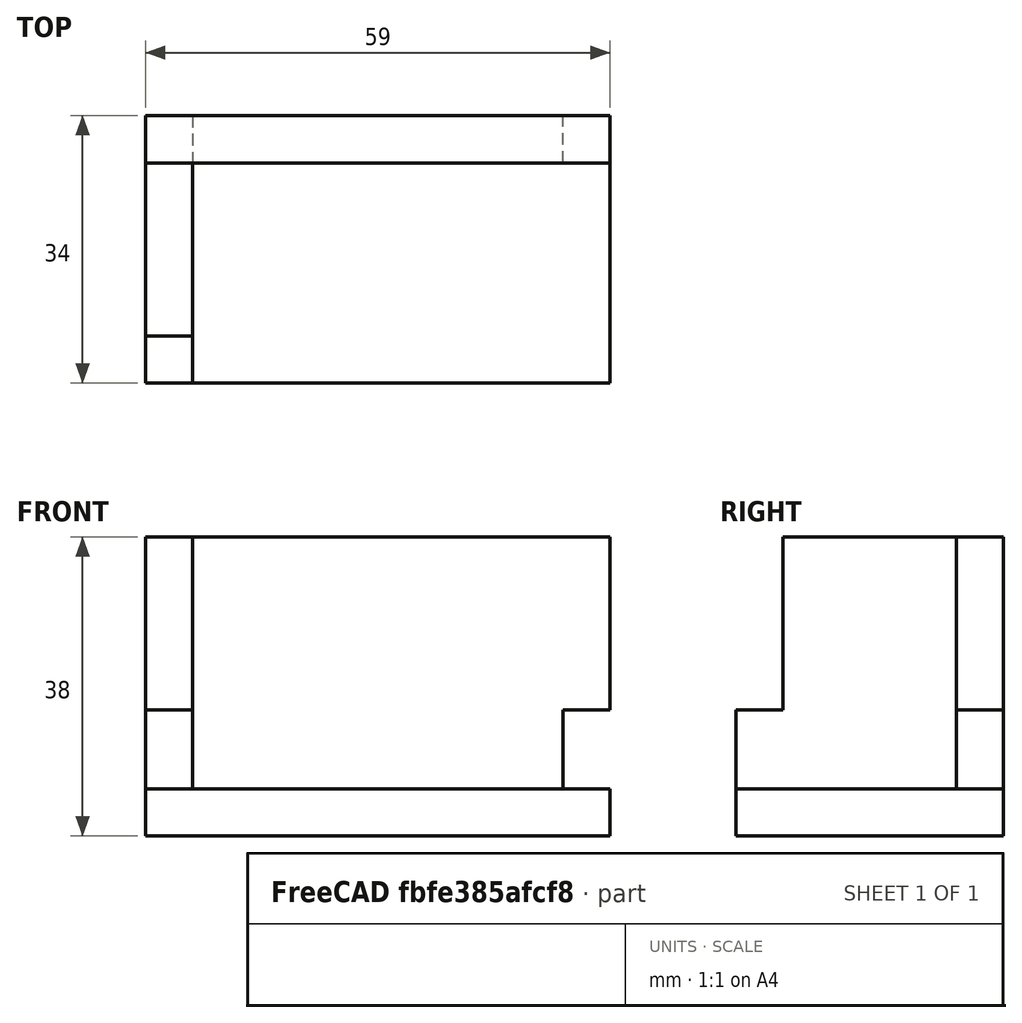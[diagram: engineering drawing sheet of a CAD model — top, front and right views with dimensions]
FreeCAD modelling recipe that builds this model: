
FCSTD DOCUMENT  (FreeCAD 0.18R16146 (Git))
Label: brass birmingham - merchant token tray
License: All rights reserved
LicenseURL: http://en.wikipedia.org/wiki/All_rights_reserved
objects: TechDraw::DrawViewPart×7, Sketcher::SketchObject×5, PartDesign::Body×5, PartDesign::Pad×3, Spreadsheet::Sheet×2, PartDesign::Pocket×2, PartDesign::FeatureBase×2, App::DocumentObjectGroup×2, TechDraw::DrawSVGTemplate×2, TechDraw::DrawViewDimension×2, TechDraw::DrawPage×2
note: 22 computed .brp shape members not serialized (recipe doc carries the construction recipe); baked Part::Feature solids carry a one-line shape summary decoded from their .brp

FEATURE [Spreadsheet::Sheet] Spreadsheet  label="my_variables"
  cells = A1=foam_width; B1(foam_width)==6mm; A2=lower_height; B2(lower_height)==29mm; A3=outer height (minus base); B3(height_adjusted)==38mm - B1; A4=outer long width; B4(width_long)==96mm; A5=outer short width; B5(width_short)==59mm
FEATURE [Sketcher::SketchObject] Sketch
  MapMode = 5
  Support = -> [XY_Plane]
  expr: Constraints[9] = my_variables001.width_short
  expr: Constraints[10] = my_variables001.width_long
  sketch-geometry (4):
    g0: LineSegment StartX=-29.5 StartY=34 StartZ=0 EndX=29.5 EndY=34 EndZ=0
    g1: LineSegment StartX=29.5 StartY=34 StartZ=0 EndX=29.5 EndY=0 EndZ=0
    g2: LineSegment StartX=29.5 StartY=0 StartZ=0 EndX=-29.5 EndY=0 EndZ=0
    g3: LineSegment StartX=-29.5 StartY=0 StartZ=0 EndX=-29.5 EndY=34 EndZ=0
  constraints (11):
    c: Coincident(g0,g1)
    c: Coincident(g1,g2)
    c: Coincident(g2,g3)
    c: Coincident(g3,g0)
    c: Horizontal(g0)
    c: Horizontal(g2)
    c: Vertical(g1)
    c: Vertical(g3)
    c: Symmetric(g2,g2,g-1)
    c: Distance(g3) = 34
    c: Distance(g2) = 59
FEATURE [PartDesign::Pad] Pad
  Length = 6
  Length2 = 100
  Profile = -> Sketch
  Type = 0
  expr: Length = my_variables.foam_width
FEATURE [PartDesign::Body] Body  label="base"
  Group = -> [Sketch,Pad]
  Origin = -> Origin
  Tip = -> Pad
FEATURE [Sketcher::SketchObject] Sketch001
  MapMode = 5
  Placement = pos=(0,0,0) rot=(1,0,0;1.5708rad)
  Support = -> [XZ_Plane001]
  expr: Constraints[10] = my_variables001.width_long
  expr: Constraints[9] = my_variables001.height_adjusted
  sketch-geometry (4):
    g0: LineSegment StartX=-29.5 StartY=32 StartZ=0 EndX=29.5 EndY=32 EndZ=0
    g1: LineSegment StartX=29.5 StartY=32 StartZ=0 EndX=29.5 EndY=0 EndZ=0
    g2: LineSegment StartX=29.5 StartY=0 StartZ=0 EndX=-29.5 EndY=0 EndZ=0
    g3: LineSegment StartX=-29.5 StartY=0 StartZ=0 EndX=-29.5 EndY=32 EndZ=0
  constraints (11):
    c: Coincident(g0,g1)
    c: Coincident(g1,g2)
    c: Coincident(g2,g3)
    c: Coincident(g3,g0)
    c: Horizontal(g0)
    c: Horizontal(g2)
    c: Vertical(g1)
    c: Vertical(g3)
    c: Symmetric(g2,g2,g-1)
    c: Distance(g3) = 32
    c: Distance(g0) = 59
FEATURE [PartDesign::Pad] Pad001
  Length = 6
  Length2 = 100
  Placement = pos=(0,0,0) rot=(1,0,0;1.5708rad)
  Profile = -> Sketch001
  Type = 0
  expr: Length = my_variables.foam_width
FEATURE [Sketcher::SketchObject] Sketch002
  MapMode = 5
  Placement = pos=(0,-6,-1.3e-15) rot=(1,0,0;1.5708rad)
  Support = -> [Pad001]
  expr: Constraints[30] = my_variables.foam_width
  expr: Constraints[29] = my_variables.foam_width
  expr: Constraints[10] = Sketch001.Constraints[10]
  expr: Constraints[9] = Sketch001.Constraints[9]
  sketch-geometry (12):
    g0: LineSegment [constr] StartX=-29.5 StartY=32 StartZ=0 EndX=29.5 EndY=32 EndZ=0
    g1: LineSegment [constr] StartX=29.5 StartY=32 StartZ=0 EndX=29.5 EndY=0 EndZ=0
    g2: LineSegment [constr] StartX=29.5 StartY=0 StartZ=0 EndX=-29.5 EndY=0 EndZ=0
    g3: LineSegment [constr] StartX=-29.5 StartY=0 StartZ=0 EndX=-29.5 EndY=32 EndZ=0
    g4: LineSegment StartX=-29.5 StartY=10 StartZ=0 EndX=-23.5 EndY=10 EndZ=0
    g5: LineSegment StartX=-23.5 StartY=10 StartZ=0 EndX=-23.5 EndY=0 EndZ=0
    g6: LineSegment StartX=-23.5 StartY=0 StartZ=0 EndX=-29.5 EndY=0 EndZ=0
    g7: LineSegment StartX=-29.5 StartY=0 StartZ=0 EndX=-29.5 EndY=10 EndZ=0
    g8: LineSegment StartX=23.5 StartY=10 StartZ=0 EndX=29.5 EndY=10 EndZ=0
    g9: LineSegment StartX=29.5 StartY=10 StartZ=0 EndX=29.5 EndY=0 EndZ=0
    g10: LineSegment StartX=29.5 StartY=0 StartZ=0 EndX=23.5 EndY=0 EndZ=0
    g11: LineSegment StartX=23.5 StartY=0 StartZ=0 EndX=23.5 EndY=10 EndZ=0
  constraints (33):
    c: Coincident(g0,g1)
    c: Coincident(g1,g2)
    c: Coincident(g2,g3)
    c: Coincident(g3,g0)
    c: Horizontal(g0)
    c: Horizontal(g2)
    c: Vertical(g1)
    c: Vertical(g3)
    c: Symmetric(g2,g2,g-1)
    c: Distance(g3) = 32
    c: Distance(g0) = 59
    c: Coincident(g4,g5)
    c: Coincident(g5,g6)
    c: Coincident(g6,g7)
    c: Coincident(g7,g4)
    c: Horizontal(g4)
    c: Horizontal(g6)
    c: Vertical(g5)
    c: Vertical(g7)
    c: Coincident(g8,g9)
    c: Coincident(g9,g10)
    c: Coincident(g10,g11)
    c: Coincident(g11,g8)
    c: Horizontal(g8)
    c: Horizontal(g10)
    c: Vertical(g9)
    c: Vertical(g11)
    c: Coincident(g6,g2)
    c: Coincident(g9,g1)
    c: Distance(g4) = 6
    c: Distance(g8) = 6
    c: Distance(g5) = 10
    c: Distance(g11) = 10
FEATURE [PartDesign::Pocket] Pocket
  BaseFeature = -> Pad001
  Length = 5
  Length2 = 100
  Placement = pos=(0,0,0) rot=(1,0,0;1.5708rad)
  Profile = -> Sketch002
  Type = 1
FEATURE [PartDesign::Body] Body001  label="side long"
  Group = -> [Sketch001,Pad001,Sketch002,Pocket]
  Origin = -> Origin001
  Placement = pos=(7e-15,6,6) rot=(0,0,1;0rad)
  Tip = -> Pocket
FEATURE [PartDesign::FeatureBase] Clone
  BaseFeature = -> Body001
  Placement = pos=(7e-15,6,6) rot=(0,0,1;0rad)
FEATURE [PartDesign::Body] Body002  label="side long - clone"
  BaseFeature = -> Body001
  Group = -> [Clone]
  Origin = -> Origin002
  Placement = pos=(-1.4e-14,28,-1.28e-14) rot=(0,0,1;0rad)
  Tip = -> Clone
FEATURE [Sketcher::SketchObject] Sketch003
  MapMode = 5
  Placement = pos=(0,0,0) rot=(0.57735,0.57735,0.57735;2.0944rad)
  Support = -> [YZ_Plane003]
  expr: Constraints[10] = my_variables001.width_short
  expr: Constraints[9] = my_variables001.height_adjusted
  sketch-geometry (4):
    g0: LineSegment StartX=-17 StartY=32 StartZ=0 EndX=17 EndY=32 EndZ=0
    g1: LineSegment StartX=17 StartY=32 StartZ=0 EndX=17 EndY=0 EndZ=0
    g2: LineSegment StartX=17 StartY=0 StartZ=0 EndX=-17 EndY=0 EndZ=0
    g3: LineSegment StartX=-17 StartY=0 StartZ=0 EndX=-17 EndY=32 EndZ=0
  constraints (11):
    c: Coincident(g0,g1)
    c: Coincident(g1,g2)
    c: Coincident(g2,g3)
    c: Coincident(g3,g0)
    c: Horizontal(g0)
    c: Horizontal(g2)
    c: Vertical(g1)
    c: Vertical(g3)
    c: Symmetric(g2,g2,g-1)
    c: Distance(g3) = 32
    c: Distance(g0) = 34
FEATURE [PartDesign::Pad] Pad002
  Length = 6
  Length2 = 100
  Placement = pos=(0,0,0) rot=(0.57735,0.57735,0.57735;2.0944rad)
  Profile = -> Sketch003
  Type = 0
  expr: Length = my_variables.foam_width
FEATURE [Sketcher::SketchObject] Sketch004
  MapMode = 5
  Placement = pos=(6,-2.7e-15,2e-15) rot=(0.57735,0.57735,0.57735;2.0944rad)
  Support = -> [Pad002]
  expr: Constraints[31] = my_variables001.foam_width
  expr: Constraints[20] = my_variables001.foam_width
  expr: Constraints[9] = Sketch003.Constraints[9]
  expr: Constraints[10] = Sketch003.Constraints[10]
  sketch-geometry (12):
    g0: LineSegment [constr] StartX=-17 StartY=32 StartZ=0 EndX=17 EndY=32 EndZ=0
    g1: LineSegment [constr] StartX=17 StartY=32 StartZ=0 EndX=17 EndY=0 EndZ=0
    g2: LineSegment [constr] StartX=17 StartY=0 StartZ=0 EndX=-17 EndY=0 EndZ=0
    g3: LineSegment [constr] StartX=-17 StartY=0 StartZ=0 EndX=-17 EndY=32 EndZ=0
    g4: LineSegment StartX=11 StartY=32 StartZ=0 EndX=17 EndY=32 EndZ=0
    g5: LineSegment StartX=17 StartY=32 StartZ=0 EndX=17 EndY=10 EndZ=0
    g6: LineSegment StartX=17 StartY=10 StartZ=0 EndX=11 EndY=10 EndZ=0
    g7: LineSegment StartX=11 StartY=10 StartZ=0 EndX=11 EndY=32 EndZ=0
    g8: LineSegment StartX=-11 StartY=10 StartZ=0 EndX=-17 EndY=10 EndZ=0
    g9: LineSegment StartX=-17 StartY=10 StartZ=0 EndX=-17 EndY=32 EndZ=0
    g10: LineSegment StartX=-17 StartY=32 StartZ=0 EndX=-11 EndY=32 EndZ=0
    g11: LineSegment StartX=-11 StartY=32 StartZ=0 EndX=-11 EndY=10 EndZ=0
  constraints (33):
    c: Coincident(g0,g1)
    c: Coincident(g1,g2)
    c: Coincident(g2,g3)
    c: Coincident(g3,g0)
    c: Horizontal(g0)
    c: Horizontal(g2)
    c: Vertical(g1)
    c: Vertical(g3)
    c: Symmetric(g2,g2,g-1)
    c: Distance(g3) = 32
    c: Distance(g0) = 34
    c: Coincident(g4,g5)
    c: Coincident(g5,g6)
    c: Coincident(g6,g7)
    c: Coincident(g7,g4)
    c: Horizontal(g4)
    c: Horizontal(g6)
    c: Vertical(g5)
    c: Vertical(g7)
    c: Coincident(g4,g0)
    c: Distance(g6) = 6
    c: Distance(g5,g1) = 10
    c: Coincident(g8,g9)
    c: Coincident(g9,g10)
    c: Coincident(g10,g11)
    c: Coincident(g11,g8)
    c: Horizontal(g8)
    c: Horizontal(g10)
    c: Vertical(g9)
    c: Vertical(g11)
    c: Coincident(g9,g0)
    c: Distance(g8) = 6
    c: Distance(g8,g2) = 10
FEATURE [PartDesign::Pocket] Pocket001
  BaseFeature = -> Pad002
  Length = 5
  Length2 = 100
  Placement = pos=(0,0,0) rot=(0.57735,0.57735,0.57735;2.0944rad)
  Profile = -> Sketch004
  Type = 1
FEATURE [PartDesign::Body] Body003  label="side short"
  Group = -> [Sketch003,Pad002,Sketch004,Pocket001]
  Origin = -> Origin003
  Placement = pos=(23.5,17,6) rot=(0,0,1;0rad)
  Tip = -> Pocket001
FEATURE [App::DocumentObjectGroup] Group  label="parts"
  Group = -> [Body,Body001,Body003]
FEATURE [PartDesign::FeatureBase] Clone001
  BaseFeature = -> Body003
  Placement = pos=(34,25,6) rot=(0,0,1;0rad)
FEATURE [PartDesign::Body] Body004  label="side small - clone"
  BaseFeature = -> Body003
  Group = -> [Clone001]
  Origin = -> Origin004
  Placement = pos=(-63.5,-8,1.6e-15) rot=(0,0,1;0rad)
  Tip = -> Clone001
FEATURE [App::DocumentObjectGroup] Group001  label="clones"
  Group = -> [Body002,Body004]
FEATURE [TechDraw::DrawSVGTemplate] Template
  Height = 210
  Orientation = 1
  Width = 297
FEATURE [TechDraw::DrawViewPart] View002
  CoarseView = false
  Direction = (0,0,1)
  Focus = 100
  HardHidden = false
  IsoCount = 0
  IsoHidden = false
  IsoVisible = false
  LockPosition = false
  Perspective = false
  Rotation = 0
  ScaleType = 0
  SeamHidden = false
  SeamVisible = false
  SmoothHidden = false
  SmoothVisible = false
  Source = -> [Body]
  X = 62.9845
  Y = 172.655
FEATURE [TechDraw::DrawViewDimension] Dimension
  Arbitrary = false
  FormatSpec = %.2f
  LockPosition = false
  MeasureType = 1
  OverTolerance = 0
  References2D = -> [View002]
  Rotation = 0
  ScaleType = 0
  Type = 0
  UnderTolerance = 0
  X = -43.1289
  Y = -1.08247
FEATURE [TechDraw::DrawViewDimension] Dimension001
  Arbitrary = false
  FormatSpec = %.2f
  LockPosition = false
  MeasureType = 1
  OverTolerance = 0
  References2D = -> [View002]
  Rotation = 0
  ScaleType = 0
  Type = 0
  UnderTolerance = 0
  X = -2.43557
  Y = -27.6057
FEATURE [TechDraw::DrawViewPart] View003
  CoarseView = false
  Direction = (0,-1,0)
  Focus = 100
  HardHidden = false
  IsoCount = 0
  IsoHidden = false
  IsoVisible = false
  LockPosition = false
  Perspective = false
  Rotation = 0
  ScaleType = 0
  SeamHidden = false
  SeamVisible = false
  SmoothHidden = false
  SmoothVisible = false
  Source = -> [Body001]
  X = 62.7139
  Y = 110.954
FEATURE [Spreadsheet::Sheet] Spreadsheet001  label="my_variables001"
  cells = A1=foam_width; B1(foam_width)==6mm; A3=outer height (minus base); B3(height_adjusted)==38mm - B1; A4=outer long width; B4(width_long)==59mm; A5=outer short width; B5(width_short)==34mm
FEATURE [TechDraw::DrawViewPart] View004
  CoarseView = false
  Direction = (0,-1,0)
  Focus = 100
  HardHidden = false
  IsoCount = 0
  IsoHidden = false
  IsoVisible = false
  LockPosition = false
  Perspective = false
  Rotation = 0
  ScaleType = 0
  SeamHidden = false
  SeamVisible = false
  SmoothHidden = false
  SmoothVisible = false
  Source = -> [Body001]
  X = 62.1727
  Y = 58.4536
FEATURE [TechDraw::DrawViewPart] View005
  CoarseView = false
  Direction = (1,0,0)
  Focus = 100
  HardHidden = false
  IsoCount = 0
  IsoHidden = false
  IsoVisible = false
  LockPosition = false
  Perspective = false
  Rotation = 0
  ScaleType = 0
  SeamHidden = false
  SeamVisible = false
  SmoothHidden = false
  SmoothVisible = false
  Source = -> [Body003]
  X = 188.822
  Y = 186.997
FEATURE [TechDraw::DrawViewPart] View006
  CoarseView = false
  Direction = (1,0,0)
  Focus = 100
  HardHidden = false
  IsoCount = 0
  IsoHidden = false
  IsoVisible = false
  LockPosition = false
  Perspective = false
  Rotation = 0
  ScaleType = 0
  SeamHidden = false
  SeamVisible = false
  SmoothHidden = false
  SmoothVisible = false
  Source = -> [Body003]
  X = 188.01
  Y = 141.534
FEATURE [TechDraw::DrawSVGTemplate] Template001
  Height = 210
  Orientation = 1
  Width = 297
FEATURE [TechDraw::DrawViewPart] View
  CoarseView = false
  Direction = (0.577,-0.577,0.577)
  Focus = 100
  HardHidden = false
  IsoCount = 0
  IsoHidden = false
  IsoVisible = false
  LockPosition = false
  Perspective = false
  Rotation = 0
  Scale = 1.5
  ScaleType = 0
  SeamHidden = false
  SeamVisible = false
  SmoothHidden = false
  SmoothVisible = false
  Source = -> [Body,Body004,Body003,Body002,Body001,Group001]
  X = 149.853
  Y = 105.812
FEATURE [TechDraw::DrawPage] Page001  label="iso view"
  KeepUpdated = true
  ProjectionType = 0
  Scale = 1.5
  Template = -> Template001
  Views = -> [View]
FEATURE [TechDraw::DrawViewPart] View007
  CoarseView = false
  Direction = (0,0,1)
  Focus = 100
  HardHidden = false
  IsoCount = 0
  IsoHidden = false
  IsoVisible = false
  LockPosition = false
  Perspective = false
  Rotation = 0
  ScaleType = 0
  SeamHidden = false
  SeamVisible = false
  SmoothHidden = false
  SmoothVisible = false
  Source = -> [Body,Body004,Body003,Body002,Body001,Group001]
  X = 190.446
  Y = 89.8454
FEATURE [TechDraw::DrawPage] Page  label="Parts"
  KeepUpdated = true
  ProjectionType = 0
  Template = -> Template
  Views = -> [View002,Dimension,Dimension001,View003,View004,View005,View006,View007]
